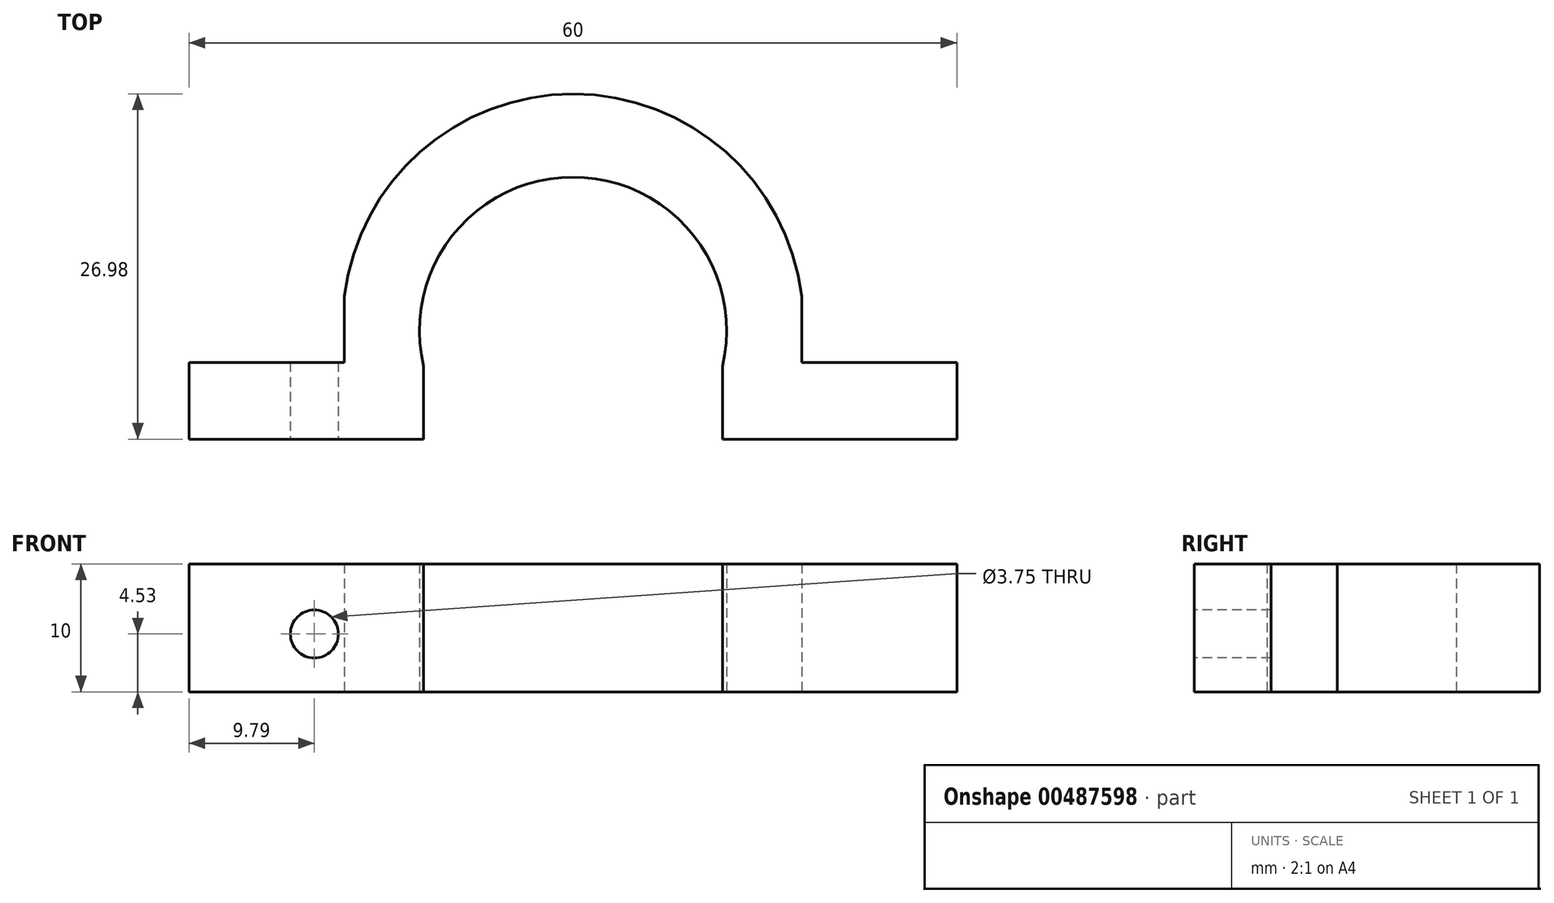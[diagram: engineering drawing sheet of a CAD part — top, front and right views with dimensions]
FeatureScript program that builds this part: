
annotation { "Feature Type Name" : "Feature", "Feature Type Description" : "" }
export const myFeature = defineFeature(function(context is Context, id is Id, definition is map)
    precondition{}
    {
        {
            var Q0;
            Q0=qCreatedBy(makeId("Top.planeOp"),FACE);
            var sketch = newSketch(context, id + "F0", { "sketchPlane" : qUnion([Q0])});
            skLineSegment(sketch, "E0", {"start": v(-17.87, 11.17) * mm, "end": v(-17.87, 6) * mm});
            skLineSegment(sketch, "E1", {"start": v(-17.87, 6) * mm, "end": v(-30, 6) * mm});
            skLineSegment(sketch, "E2", {"start": v(-30, 6) * mm, "end": v(-30, 0) * mm});
            skLineSegment(sketch, "E3", {"start": v(-30, 0) * mm, "end": v(-11.67, 0) * mm});
            skLineSegment(sketch, "E4", {"start": v(-11.67, 0) * mm, "end": v(-11.67, 5.7) * mm});
            skLineSegment(sketch, "E5.MirrorCS", {"start": v(11.67, 0) * mm, "end": v(11.67, 5.7) * mm});
            skLineSegment(sketch, "E6.MirrorCS", {"start": v(30, 0) * mm, "end": v(11.67, 0) * mm});
            skLineSegment(sketch, "E7.MirrorCS", {"start": v(17.87, 6) * mm, "end": v(30, 6) * mm});
            skLineSegment(sketch, "E8.MirrorCS", {"start": v(30, 6) * mm, "end": v(30, 0) * mm});
            skLineSegment(sketch, "E9.MirrorCS", {"start": v(17.87, 11.17) * mm, "end": v(17.87, 6) * mm});
            skArc(sketch, "E10", {"start": v(11.67, 5.7) * mm, "mid": v(0, 20.49) * mm, "end": v(-11.67, 5.7) * mm});
            skArc(sketch, "E11", {"start": v(17.87, 11.17) * mm, "mid": v(0, 26.98) * mm, "end": v(-17.87, 11.17) * mm});
            skSolve(sketch);
        }
        {
            var Q0;
            Q0=makeQuery(id+"F0.imprint","IMPRINT",FACE,{"disambiguationData":[TD([[makeQuery(id+"F0.imprint","IMPRINT",EDGE,{"derivedFrom":sQuery(id+"F0.wireOp",EDGE,"E0")}),1.0]])]});
            extrude(context, id + "F1", {"entities" : qUnion([Q0]), "depth" : 10 * mm});
        }
        {
            var Q0;
            Q0=qCreatedBy(makeId("Front.planeOp"),FACE);
            var sketch = newSketch(context, id + "F2", { "sketchPlane" : qUnion([Q0])});
            skCircle(sketch, "E12", {"center": v(-20.21, 4.53) * mm, "radius": 1.88 * mm});
            skCircle(sketch, "E13.MirrorC", {"center": v(20.21, 4.53) * mm, "radius": 1.88 * mm});
            skSolve(sketch);
        }
        {
            var Q0;
            Q0=makeQuery(id+"F2.imprint","IMPRINT",FACE,{"disambiguationData":[TD([[makeQuery(id+"F2.imprint","IMPRINT",EDGE,{"derivedFrom":sQuery(id+"F2.wireOp",EDGE,"E12")}),1.0]])]});
            var Q1;
            Q1=makeQuery(id+"F2.imprint","IMPRINT",FACE,{"disambiguationData":[TD([[makeQuery(id+"F2.imprint","IMPRINT",EDGE,{"derivedFrom":sQuery(id+"F2.wireOp",EDGE,"E13.MirrorC")}),-1.0]])]});
            var Q2;
            Q2=sQuery(id+"F2.wireOp",EDGE,"E12");
            var Q3;
            Q3=sQuery(id+"F2.wireOp",EDGE,"E13.MirrorC");
            extrude(context, id + "F3", {"entities" : qUnion([Q0, Q1]), "operationType" : NewBodyOperationType.REMOVE, "surfaceEntities" : qUnion([Q2, Q3]), "oppositeDirection" : true, "depth" : 6 * mm});
        }
    });
